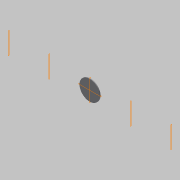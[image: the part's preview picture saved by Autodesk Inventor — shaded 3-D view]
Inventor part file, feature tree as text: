
AUTODESK INVENTOR PART (.ipt)
format: ipt  version: 2017.3 (Build 213257000, 257)  size: 96,768 bytes
history: native  units: in
note: dims shown in document units (in); Inventor stores cm internally (conversion verified against a paired STEP export)
features: plane x7, extrude x1, sketch x1, other x1
ambient origin geometry x8: Origin, YZ Plane, XZ Plane, XY Plane, X Axis, Y Axis, Z Axis, Center Point
bodies: Solid1 (feature_tree)
feature tree (10):
  plane  "Work Plane1 Centerline at surface"
  plane  "Work Plane2 Centerline at centerline"
  plane  "Work Plane3 Top"
  plane  "Work Plane4 Right"
  plane  "Work Plane5 Left"
  plane  "Work Plane6 Bottom (right)"
  plane  "Work Plane7 Bottom (left)"
  extrude  "Extrusion1"  Depth=0.5in TaperAngle=0.0deg
  sketch  "Sketch1"  dims[d0=0.0in d1=141.7323in d2=0.5in d3=0.0in d4=0.0in d5=0.0in d6=0.0in d7=26.7035in d8=-26.7035in d9=53.4071in d10=-53.4071in d11=6.5in d12=53.4071in]
  other  "2D Equation Curve1"
